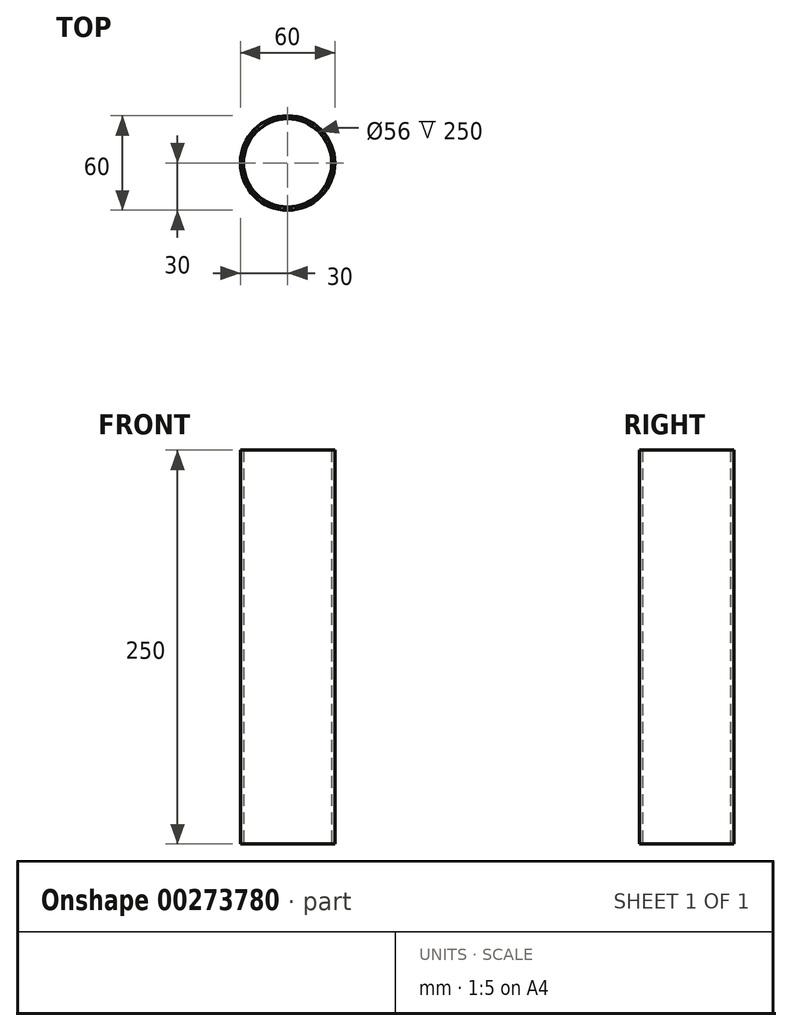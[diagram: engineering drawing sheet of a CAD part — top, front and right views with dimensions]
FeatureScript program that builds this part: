
annotation { "Feature Type Name" : "Feature", "Feature Type Description" : "" }
export const myFeature = defineFeature(function(context is Context, id is Id, definition is map)
    precondition{}
    {
        {
            var Q0;
            Q0=qCreatedBy(makeId("Top.planeOp"),FACE);
            var sketch = newSketch(context, id + "F0", { "sketchPlane" : qUnion([Q0])});
            skCircle(sketch, "E0", {"center": v(0, 0) * mm, "radius": 30 * mm});
            skCircle(sketch, "E1", {"center": v(0, 0) * mm, "radius": 28 * mm});
            skSolve(sketch);
        }
        {
            var Q0;
            Q0 = qSketchRegion(id + "F0", true);
            extrude(context, id + "F1", {"entities" : qUnion([Q0]), "depth" : 250 * mm});
        }
    });
